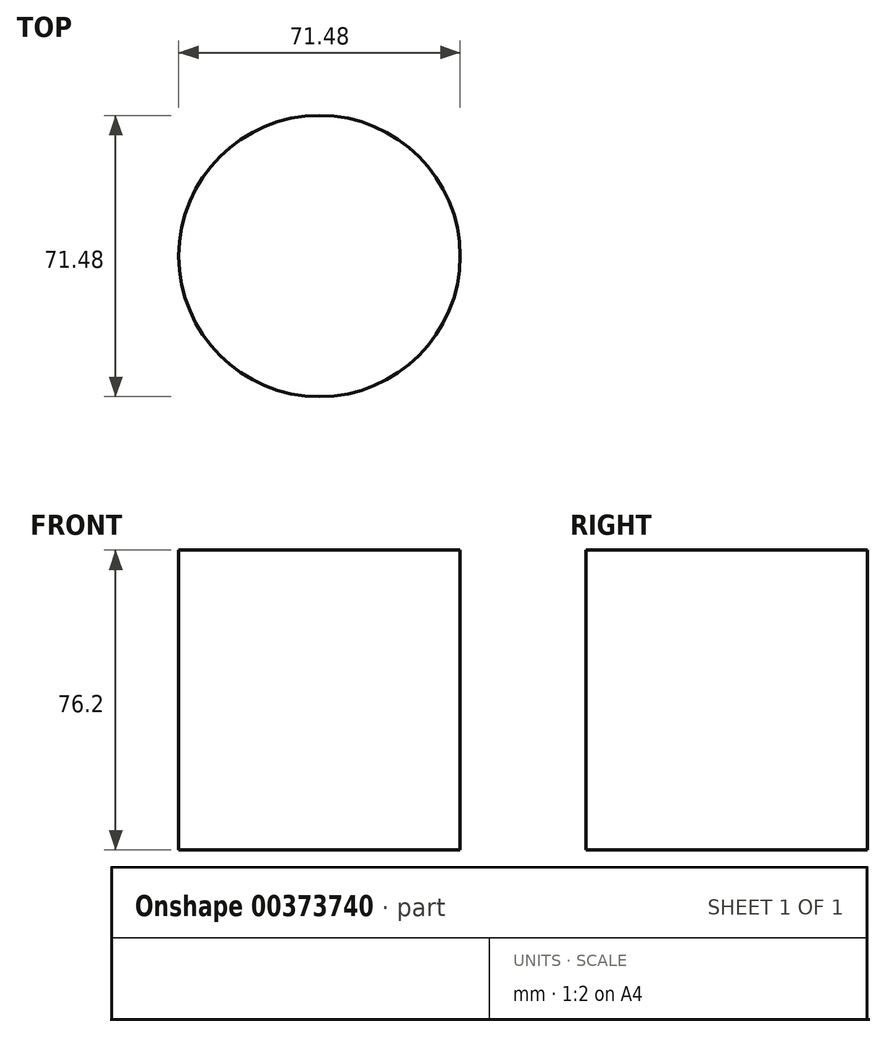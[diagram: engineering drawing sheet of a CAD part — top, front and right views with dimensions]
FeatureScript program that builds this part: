
annotation { "Feature Type Name" : "Feature", "Feature Type Description" : "" }
export const myFeature = defineFeature(function(context is Context, id is Id, definition is map)
    precondition{}
    {
        {
            var Q0;
            Q0=qCreatedBy(makeId("Top.planeOp"),FACE);
            var sketch = newSketch(context, id + "F0", { "sketchPlane" : qUnion([Q0])});
            skCircle(sketch, "E0", {"center": v(0, 0) * mm, "radius": 35.74 * mm});
            skSolve(sketch);
        }
        {
            var Q0;
            Q0 = qSketchRegion(id + "F0", true);
            extrude(context, id + "F1", {"entities" : qUnion([Q0]), "depth" : 76.2 * mm});
        }
    });
